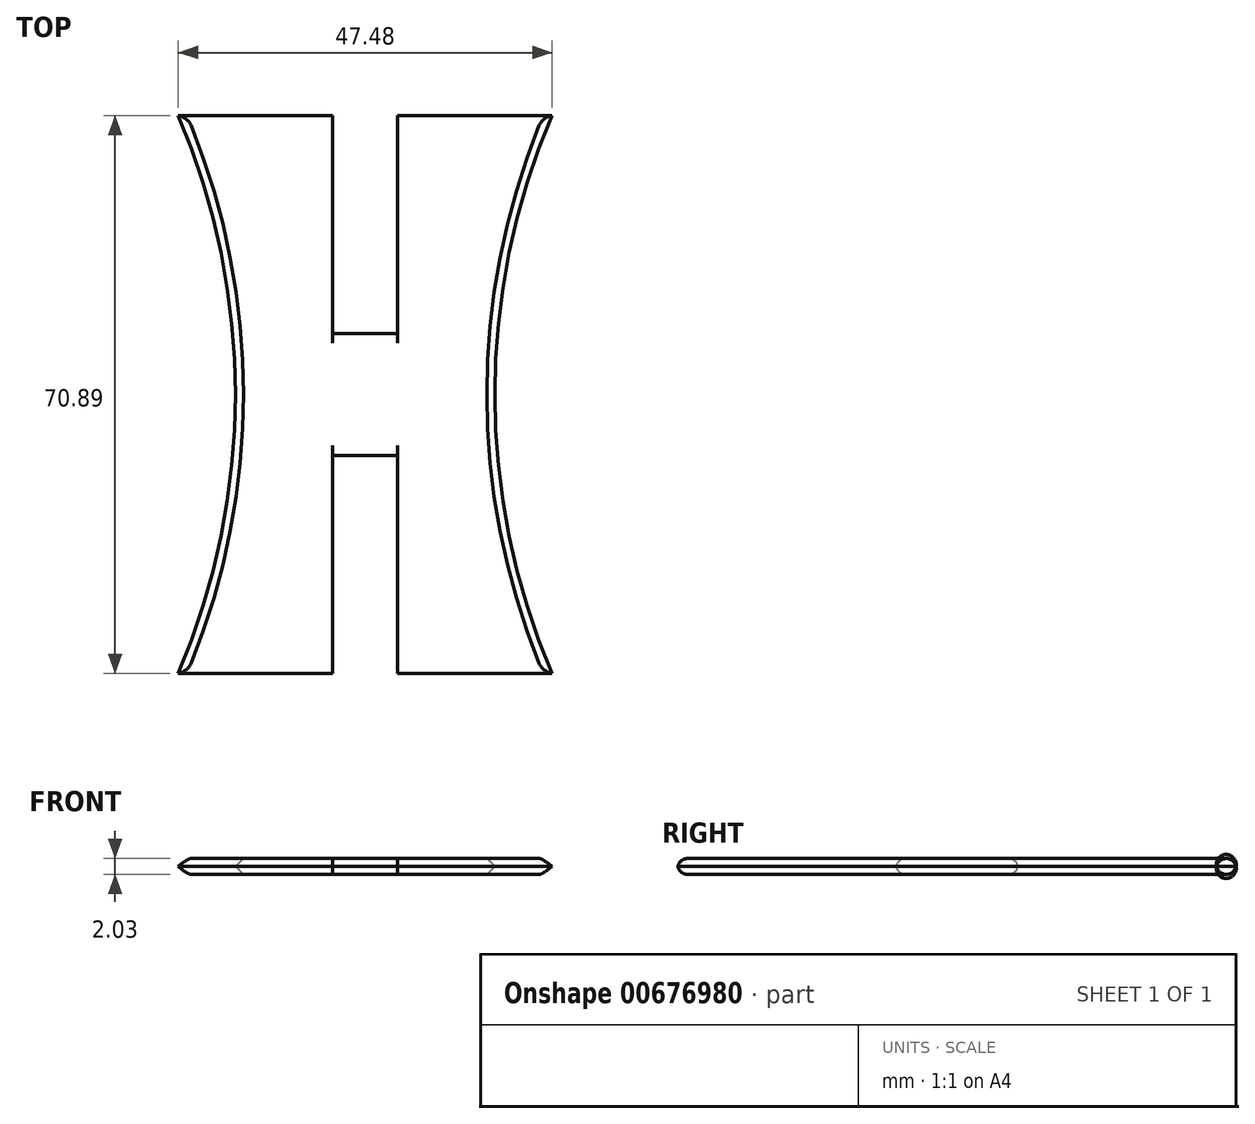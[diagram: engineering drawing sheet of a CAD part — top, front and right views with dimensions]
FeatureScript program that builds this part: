
annotation { "Feature Type Name" : "Feature", "Feature Type Description" : "" }
export const myFeature = defineFeature(function(context is Context, id is Id, definition is map)
    precondition{}
    {
        {
            var Q0;
            Q0=qCreatedBy(makeId("Top.planeOp"),FACE);
            var sketch = newSketch(context, id + "F0", { "sketchPlane" : qUnion([Q0])});
            skLineSegment(sketch, "E0.bottom", {"start": v(-24.05, 54.82) * mm, "end": v(-4.13, 54.82) * mm});
            skLineSegment(sketch, "E0.top", {"start": v(-24.05, -16.12) * mm, "end": v(-24.03, -16.12) * mm});
            skPoint(sketch, "E0.middle", {"position": v(0, 19.35) * mm});
            skArc(sketch, "E1", {"start": v(-16.73, 19.35) * mm, "mid": v(-18.58, 37.46) * mm, "end": v(-24.03, 54.82) * mm});
            skPoint(sketch, "E2.orphan", {"position": v(24.05, -16.12) * mm});
            skPoint(sketch, "E3.orphan", {"position": v(24.05, 54.82) * mm});
            skArc(sketch, "E4.MirrorCS", {"start": v(16.73, 19.35) * mm, "mid": v(18.58, 37.46) * mm, "end": v(24.03, 54.82) * mm});
            skLineSegment(sketch, "E5.MirrorCS", {"start": v(24.05, 54.82) * mm, "end": v(4.13, 54.82) * mm});
            skLineSegment(sketch, "E6.MirrorCS", {"start": v(24.05, -16.12) * mm, "end": v(24.03, -16.12) * mm});
            skLineSegment(sketch, "E7.bottom", {"start": v(-4.13, 27.13) * mm, "end": v(4.13, 27.13) * mm});
            skLineSegment(sketch, "E7.top", {"start": v(-4.13, 82.52) * mm, "end": v(4.13, 82.52) * mm});
            skLineSegment(sketch, "E7.left", {"start": v(-4.13, 27.13) * mm, "end": v(-4.13, 54.82) * mm});
            skLineSegment(sketch, "E7.right", {"start": v(4.13, 27.13) * mm, "end": v(4.13, 54.82) * mm});
            skPoint(sketch, "E7.middle", {"position": v(0, 54.82) * mm});
            skPoint(sketch, "E8.orphan", {"position": v(-24.03, -16.12) * mm});
            skPoint(sketch, "E9.orphan", {"position": v(0, -16.12) * mm});
            skArc(sketch, "E10.MirrorCS", {"start": v(-16.73, 19.35) * mm, "mid": v(-18.58, 1.25) * mm, "end": v(-24.03, -16.12) * mm});
            skLineSegment(sketch, "E11.MirrorCS", {"start": v(-24.05, -16.12) * mm, "end": v(-4.13, -16.12) * mm});
            skLineSegment(sketch, "E12.MirrorCS", {"start": v(-4.13, 11.58) * mm, "end": v(-4.13, -16.12) * mm});
            skLineSegment(sketch, "E13.MirrorCS", {"start": v(-4.13, 11.58) * mm, "end": v(4.13, 11.58) * mm});
            skLineSegment(sketch, "E14.MirrorCS", {"start": v(4.13, 11.58) * mm, "end": v(4.13, -16.12) * mm});
            skArc(sketch, "E15.MirrorCS", {"start": v(16.73, 19.35) * mm, "mid": v(18.58, 1.25) * mm, "end": v(24.03, -16.12) * mm});
            skLineSegment(sketch, "E16.MirrorCS", {"start": v(24.05, -16.12) * mm, "end": v(4.13, -16.12) * mm});
            skPoint(sketch, "E17.orphan", {"position": v(4.13, -43.81) * mm});
            skPoint(sketch, "E18.orphan", {"position": v(-4.13, -43.81) * mm});
            skSolve(sketch);
        }
        {
            var Q0;
            {var subQ6=sQuery(id+"F0.wireOp",EDGE,"E1");Q0=makeQuery(id+"F0.imprint","IMPRINT",FACE,{"disambiguationData":[TD([[makeQuery(id+"F0.imprint","IMPRINT",EDGE,{"derivedFrom":subQ6}),-1.0]])]});}
            extrude(context, id + "F1", {"entities" : qUnion([Q0]), "depth" : 2.03 * mm, "offsetDistance" : 25.4 * mm});
        }
        {
            var Q0;
            Q0=makeQuery(id+"F1.opExtrude","CAP_EDGE",EDGE,{"disambiguationData":[OSD([sQuery(id+"F0.wireOp",EDGE,"E4.MirrorCS"),sQuery(id+"F0.wireOp",EDGE,"E15.MirrorCS")])],"isStart":false});
            var Q1;
            Q1=makeQuery(id+"F1.opExtrude","CAP_EDGE",EDGE,{"disambiguationData":[OSD([sQuery(id+"F0.wireOp",EDGE,"E4.MirrorCS"),sQuery(id+"F0.wireOp",EDGE,"E15.MirrorCS")])],"isStart":true});
            var Q2;
            Q2=makeQuery(id+"F1.opExtrude","CAP_EDGE",EDGE,{"disambiguationData":[OSD([sQuery(id+"F0.wireOp",EDGE,"E1"),sQuery(id+"F0.wireOp",EDGE,"E10.MirrorCS")])],"isStart":false});
            var Q3;
            Q3=makeQuery(id+"F1.opExtrude","CAP_EDGE",EDGE,{"disambiguationData":[OSD([sQuery(id+"F0.wireOp",EDGE,"E1"),sQuery(id+"F0.wireOp",EDGE,"E10.MirrorCS")])],"isStart":true});
            chamfer(context, id + "F2", {"entities" : qUnion([Q0, Q1, Q2, Q3]), "width" : 1.27 * mm, "tangentPropagation" : true});
        }
        {
            var Q0;
            Q0=makeQuery(id+"F1.opExtrude","CAP_EDGE",EDGE,{"disambiguationData":[OSD([sQuery(id+"F0.wireOp",EDGE,"E0.bottom")])],"isStart":true});
            var Q1;
            Q1=makeQuery(id+"F1.opExtrude","CAP_EDGE",EDGE,{"disambiguationData":[OSD([sQuery(id+"F0.wireOp",EDGE,"E0.bottom")])],"isStart":false});
            var Q2;
            Q2=makeQuery(id+"F1.opExtrude","CAP_EDGE",EDGE,{"disambiguationData":[OSD([sQuery(id+"F0.wireOp",EDGE,"E5.MirrorCS")])],"isStart":false});
            var Q3;
            Q3=makeQuery(id+"F1.opExtrude","CAP_EDGE",EDGE,{"disambiguationData":[OSD([sQuery(id+"F0.wireOp",EDGE,"E5.MirrorCS")])],"isStart":true});
            var Q4;
            Q4=makeQuery(id+"F1.opExtrude","CAP_EDGE",EDGE,{"disambiguationData":[OSD([sQuery(id+"F0.wireOp",EDGE,"E16.MirrorCS")])],"isStart":false});
            var Q5;
            Q5=makeQuery(id+"F1.opExtrude","CAP_EDGE",EDGE,{"disambiguationData":[OSD([sQuery(id+"F0.wireOp",EDGE,"E16.MirrorCS")])],"isStart":true});
            var Q6;
            Q6=makeQuery(id+"F1.opExtrude","CAP_EDGE",EDGE,{"disambiguationData":[OSD([sQuery(id+"F0.wireOp",EDGE,"E11.MirrorCS")])],"isStart":false});
            var Q7;
            Q7=makeQuery(id+"F1.opExtrude","CAP_EDGE",EDGE,{"disambiguationData":[OSD([sQuery(id+"F0.wireOp",EDGE,"E11.MirrorCS")])],"isStart":true});
            var Q8;
            Q8=makeQuery(id+"F1.opExtrude","CAP_EDGE",EDGE,{"disambiguationData":[OSD([sQuery(id+"F0.wireOp",EDGE,"E13.MirrorCS")])],"isStart":false});
            var Q9;
            Q9=makeQuery(id+"F1.opExtrude","CAP_EDGE",EDGE,{"disambiguationData":[OSD([sQuery(id+"F0.wireOp",EDGE,"E13.MirrorCS")])],"isStart":true});
            var Q10;
            Q10=makeQuery(id+"F1.opExtrude","CAP_EDGE",EDGE,{"disambiguationData":[OSD([sQuery(id+"F0.wireOp",EDGE,"E7.bottom")])],"isStart":true});
            var Q11;
            Q11=makeQuery(id+"F1.opExtrude","CAP_EDGE",EDGE,{"disambiguationData":[OSD([sQuery(id+"F0.wireOp",EDGE,"E7.bottom")])],"isStart":false});
            fillet(context, id + "F3", {"entities" : qUnion([Q0, Q1, Q2, Q3, Q4, Q5, Q6, Q7, Q8, Q9, Q10, Q11]), "radius" : 1.27 * mm, "tangentPropagation" : true, "allowEdgeOverflow" : false});
        }
    });
